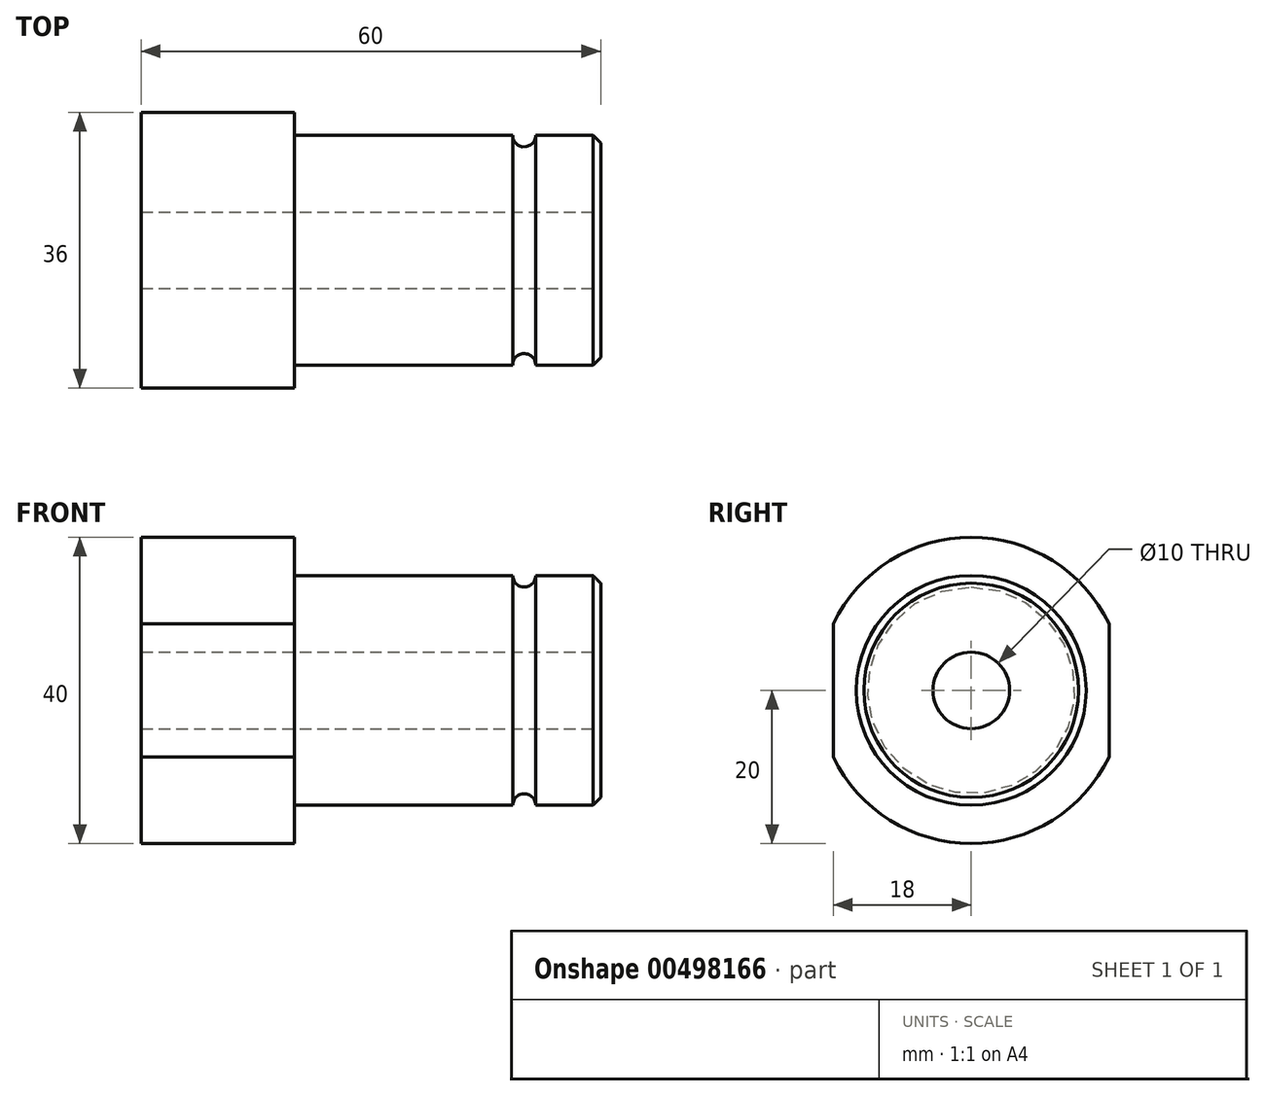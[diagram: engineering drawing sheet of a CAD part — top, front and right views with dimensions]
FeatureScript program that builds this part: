
annotation { "Feature Type Name" : "Feature", "Feature Type Description" : "" }
export const myFeature = defineFeature(function(context is Context, id is Id, definition is map)
    precondition{}
    {
        {
            var Q0;
            Q0=qCreatedBy(makeId("Front.planeOp"),FACE);
            var sketch = newSketch(context, id + "F0", { "sketchPlane" : qUnion([Q0])});
            skLineSegment(sketch, "E0", {"start": v(0, 0) * mm, "end": v(0, 20) * mm});
            skLineSegment(sketch, "E1", {"start": v(0, 20) * mm, "end": v(20, 20) * mm});
            skLineSegment(sketch, "E2", {"start": v(20, 20) * mm, "end": v(20, 15) * mm});
            skLineSegment(sketch, "E3", {"start": v(20, 15) * mm, "end": v(60, 15) * mm});
            skLineSegment(sketch, "E4", {"start": v(60, 15) * mm, "end": v(60, 0) * mm});
            skLineSegment(sketch, "E5", {"start": v(60, 0) * mm, "end": v(0, 0) * mm});
            skLineSegment(sketch, "E6", {"start": v(69.86, 0) * mm, "end": v(-7.51, 0) * mm, "construction": true});
            skSolve(sketch);
        }
        {
            var Q0;
            Q0 = qSketchRegion(id + "F0", true);
            var Q1;
            Q1=sQuery(id+"F0.wireOp",EDGE,"E6");
            revolve(context, id + "F1", {"entities" : qUnion([Q0]), "axis" : qUnion([Q1]), "revolveType" : RevolveType.FULL});
        }
        {
            var Q0;
            Q0=makeQuery(id+"F1.opRevolve","SWEPT_FACE",FACE,{"disambiguationData":[OSD([sQuery(id+"F0.wireOp",EDGE,"E4")])]});
            var sketch = newSketch(context, id + "F2", { "sketchPlane" : qUnion([Q0])});
            skCircle(sketch, "E7", {"center": v(0, 0) * mm, "radius": 5 * mm});
            skSolve(sketch);
        }
        {
            var Q0;
            Q0 = qSketchRegion(id + "F2", true);
            extrude(context, id + "F3", {"entities" : qUnion([Q0]), "operationType" : NewBodyOperationType.REMOVE, "endBound" : BoundingType.THROUGH_ALL, "oppositeDirection" : true, "depth" : 25 * mm});
        }
        {
            var Q0;
            Q0=makeQuery(id+"F1.opRevolve","SWEPT_EDGE",EDGE,{"disambiguationData":[OSD([sQuery(id+"F0.wireOp",EDGE,"E3"),sQuery(id+"F0.wireOp",EDGE,"E4")])]});
            chamfer(context, id + "F4", {"entities" : qUnion([Q0]), "width" : 1 * mm, "tangentPropagation" : true});
        }
        {
            var Q0;
            Q0=qCreatedBy(makeId("Front.planeOp"),FACE);
            var sketch = newSketch(context, id + "F5", { "sketchPlane" : qUnion([Q0])});
            skCircle(sketch, "E8", {"center": v(50, 15) * mm, "radius": 1.5 * mm});
            skSolve(sketch);
        }
        {
            var Q0;
            Q0 = qSketchRegion(id + "F5", true);
            var Q1;
            Q1=sQuery(id+"F0.wireOp",EDGE,"E6");
            revolve(context, id + "F6", {"operationType" : NewBodyOperationType.REMOVE, "entities" : qUnion([Q0]), "axis" : qUnion([Q1]), "revolveType" : RevolveType.FULL, "oppositeDirection" : true});
        }
        {
            var Q0;
            Q0=makeQuery(id+"F1.opRevolve","SWEPT_FACE",FACE,{"disambiguationData":[OSD([sQuery(id+"F0.wireOp",EDGE,"E0")])]});
            var sketch = newSketch(context, id + "F7", { "sketchPlane" : qUnion([Q0])});
            skLineSegment(sketch, "E9.bottom", {"start": v(18, 42.81) * mm, "end": v(-18, 42.81) * mm});
            skLineSegment(sketch, "E9.top", {"start": v(18, -42.81) * mm, "end": v(-18, -42.81) * mm});
            skLineSegment(sketch, "E9.left", {"start": v(18, 42.81) * mm, "end": v(18, -42.81) * mm});
            skLineSegment(sketch, "E9.right", {"start": v(-18, 42.81) * mm, "end": v(-18, -42.81) * mm});
            skPoint(sketch, "E9.middle", {"position": v(0, 0) * mm});
            skSolve(sketch);
        }
        {
            var Q0;
            Q0=makeQuery(id+"F7.imprint","IMPRINT",FACE,{"disambiguationData":[TD([[makeQuery(id+"F7.imprint","IMPRINT",EDGE,{"derivedFrom":makeQuery(id+"F3.boolean.opBoolean","INTERSECT",EDGE,{"derivedFrom":[makeQuery(id+"F1.opRevolve","SWEPT_FACE",FACE,{"disambiguationData":[OSD([sQuery(id+"F0.wireOp",EDGE,"E0")])]}),makeQuery(id+"F3.opExtrude","SWEPT_FACE",FACE,{"disambiguationData":[OSD([sQuery(id+"F2.wireOp",EDGE,"E7")])]})]})}),-1.0]])]});
            var Q1;
            {var subQ0=sQuery(id+"F7.wireOp",EDGE,"E9.bottom");Q1=makeQuery(id+"F7.imprint","IMPRINT",FACE,{"disambiguationData":[TD([[makeQuery(id+"F7.imprint","IMPRINT",EDGE,{"derivedFrom":subQ0}),1.0]])]});}
            var Q2;
            {var subQ0=sQuery(id+"F7.wireOp",EDGE,"E9.top");Q2=makeQuery(id+"F7.imprint","IMPRINT",FACE,{"disambiguationData":[TD([[makeQuery(id+"F7.imprint","IMPRINT",EDGE,{"derivedFrom":subQ0}),-1.0]])]});}
            var Q3;
            {var subQ0=sQuery(id+"F7.wireOp",EDGE,"E9.left");var subQ1=makeQuery(id+"F1.opRevolve","SWEPT_EDGE",EDGE,{"disambiguationData":[OSD([sQuery(id+"F0.wireOp",EDGE,"E0"),sQuery(id+"F0.wireOp",EDGE,"E1")])]});var subQ2=makeQuery(id+"F7.imprint","INTERSECT",VERTEX,{"disambiguationData":[OD(0.0)],"derivedFrom":[subQ1,subQ0]});Q3=makeQuery(id+"F7.imprint","IMPRINT",FACE,{"disambiguationData":[TD([[makeQuery(id+"F7.imprint","IMPRINT",EDGE,{"disambiguationData":[TD([[subQ2,-1.0]])],"derivedFrom":subQ0}),1.0]])]});}
            var Q4;
            {var subQ0=sQuery(id+"F7.wireOp",EDGE,"E9.right");var subQ1=makeQuery(id+"F1.opRevolve","SWEPT_EDGE",EDGE,{"disambiguationData":[OSD([sQuery(id+"F0.wireOp",EDGE,"E0"),sQuery(id+"F0.wireOp",EDGE,"E1")])]});var subQ2=makeQuery(id+"F7.imprint","INTERSECT",VERTEX,{"disambiguationData":[OD(0.0)],"derivedFrom":[subQ1,subQ0]});Q4=makeQuery(id+"F7.imprint","IMPRINT",FACE,{"disambiguationData":[TD([[makeQuery(id+"F7.imprint","IMPRINT",EDGE,{"disambiguationData":[TD([[subQ2,-1.0]])],"derivedFrom":subQ0}),-1.0]])]});}
            var Q5;
            Q5=makeQuery(id+"F1.opRevolve","SWEPT_FACE",FACE,{"disambiguationData":[OSD([sQuery(id+"F0.wireOp",EDGE,"E2")])]});
            extrude(context, id + "F8", {"entities" : qUnion([Q0, Q1, Q2, Q3, Q4]), "operationType" : NewBodyOperationType.REMOVE, "endBound" : BoundingType.UP_TO_SURFACE, "oppositeDirection" : true, "depth" : 25 * mm, "endBoundEntityFace" : qUnion([Q5]), "offsetDistance" : 25 * mm});
        }
    });
